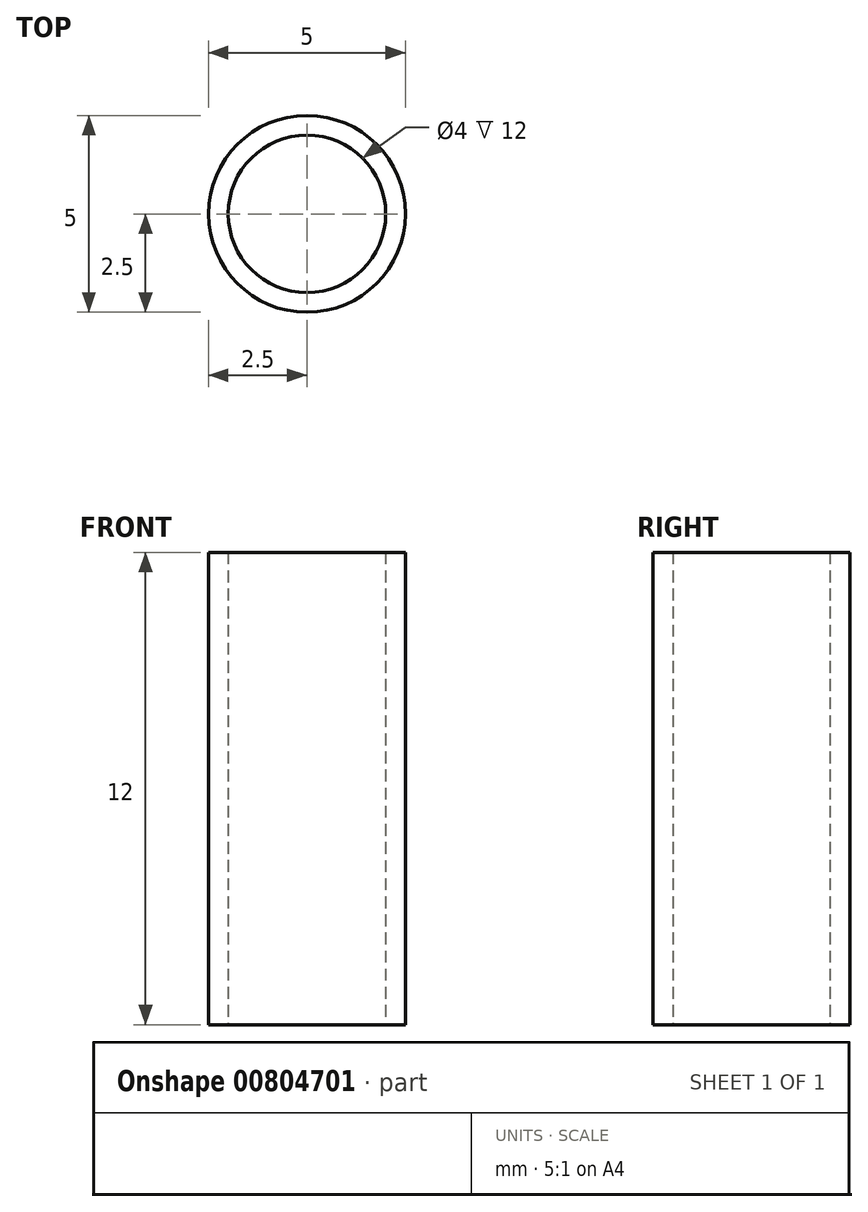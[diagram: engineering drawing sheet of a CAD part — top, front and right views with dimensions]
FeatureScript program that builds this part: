
annotation { "Feature Type Name" : "Feature", "Feature Type Description" : "" }
export const myFeature = defineFeature(function(context is Context, id is Id, definition is map)
    precondition{}
    {
        {
            var Q0;
            Q0=qCreatedBy(makeId("Top.planeOp"),FACE);
            var sketch = newSketch(context, id + "F0", { "sketchPlane" : qUnion([Q0])});
            skCircle(sketch, "E0", {"center": v(0, 0) * mm, "radius": 2 * mm});
            skCircle(sketch, "E1", {"center": v(0, 0) * mm, "radius": 2.5 * mm});
            skSolve(sketch);
        }
        {
            var Q0;
            Q0=qSketchRegion(id+"F0",true);
            extrude(context, id + "F1", {"entities" : qUnion([Q0]), "depth" : 12 * mm, "offsetDistance" : 25 * mm});
        }
    });
